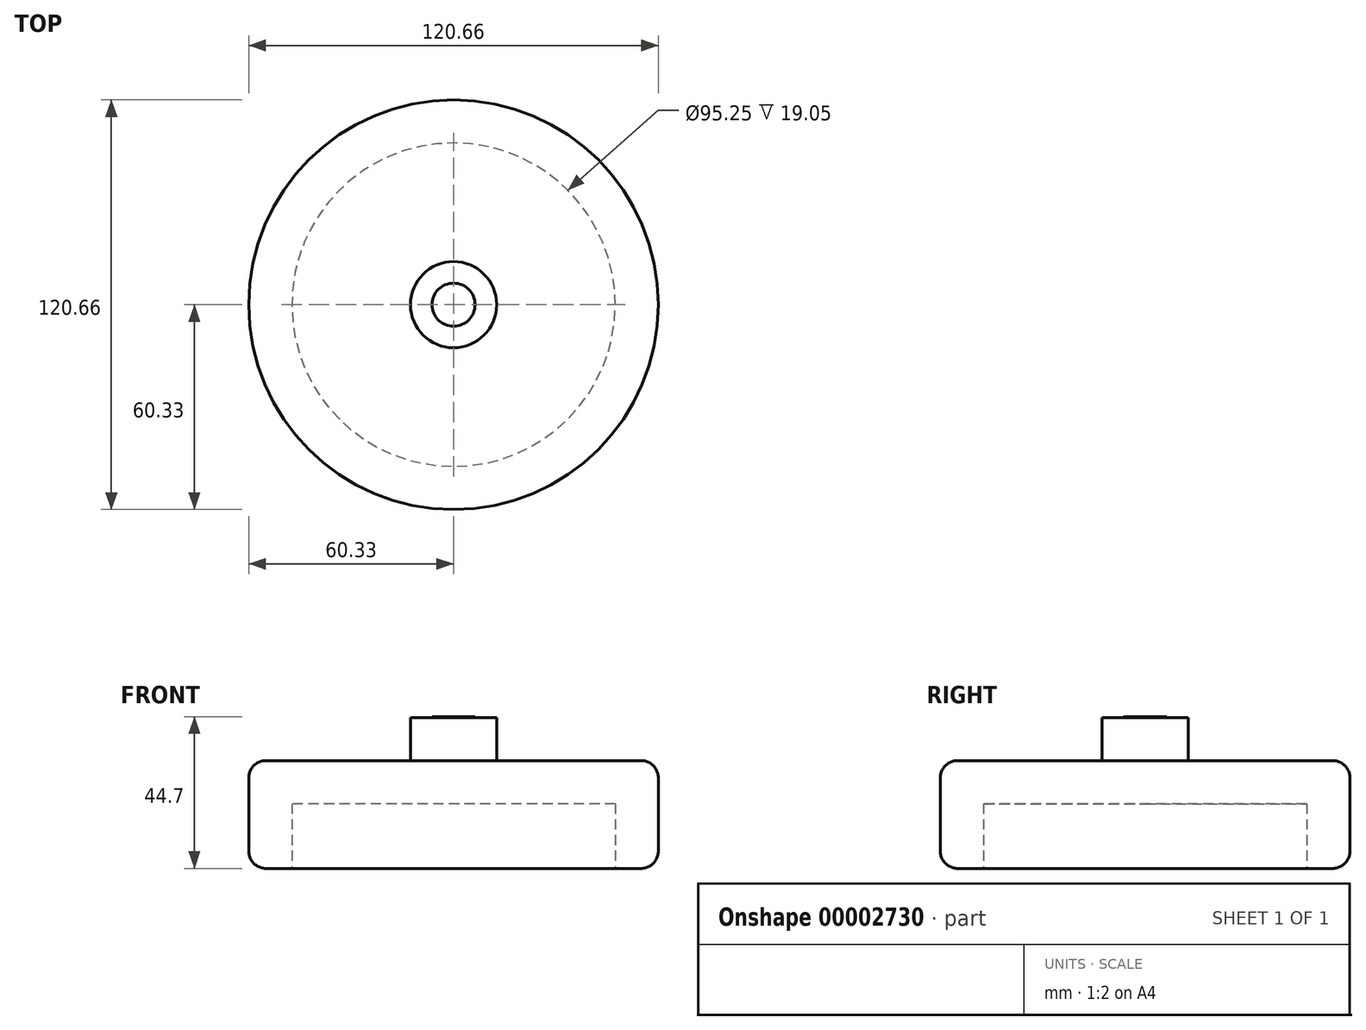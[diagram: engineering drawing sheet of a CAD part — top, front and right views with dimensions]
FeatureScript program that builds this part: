
annotation { "Feature Type Name" : "Feature", "Feature Type Description" : "" }
export const myFeature = defineFeature(function(context is Context, id is Id, definition is map)
    precondition{}
    {
        {
            var Q0;
            Q0=qCreatedBy(makeId("Top.planeOp"),FACE);
            var sketch = newSketch(context, id + "F0", { "sketchPlane" : qUnion([Q0])});
            skCircle(sketch, "E0", {"center": v(0, 0) * mm, "radius": 60.33 * mm});
            skSolve(sketch);
        }
        {
            var Q0;
            Q0=qCreatedBy(makeId("Top.planeOp"),FACE);
            var sketch = newSketch(context, id + "F1", { "sketchPlane" : qUnion([Q0])});
            skCircle(sketch, "E1", {"center": v(0, 0) * mm, "radius": 12.7 * mm});
            skSolve(sketch);
        }
        {
            var Q0;
            Q0=qCreatedBy(makeId("Top.planeOp"),FACE);
            var sketch = newSketch(context, id + "F2", { "sketchPlane" : qUnion([Q0])});
            skCircle(sketch, "E2", {"center": v(0, 0) * mm, "radius": 6.35 * mm});
            skSolve(sketch);
        }
        {
            var Q0;
            Q0=makeQuery(id+"F0.imprint","IMPRINT",FACE,{"disambiguationData":[TD([[makeQuery(id+"F0.imprint","IMPRINT",EDGE,{"derivedFrom":sQuery(id+"F0.wireOp",EDGE,"E0")}),1.0]])]});
            extrude(context, id + "F3", {"entities" : qUnion([Q0]), "depth" : 31.75 * mm});
        }
        {
            var Q0;
            Q0=makeQuery(id+"F1.imprint","IMPRINT",FACE,{"disambiguationData":[TD([[makeQuery(id+"F1.imprint","IMPRINT",EDGE,{"derivedFrom":sQuery(id+"F1.wireOp",EDGE,"E1")}),1.0]])]});
            extrude(context, id + "F4", {"entities" : qUnion([Q0]), "operationType" : NewBodyOperationType.ADD, "depth" : 44.45 * mm});
        }
        {
            var Q0;
            Q0=makeQuery(id+"F2.imprint","IMPRINT",FACE,{"disambiguationData":[TD([[makeQuery(id+"F2.imprint","IMPRINT",EDGE,{"derivedFrom":sQuery(id+"F2.wireOp",EDGE,"E2")}),1.0]])]});
            extrude(context, id + "F5", {"entities" : qUnion([Q0]), "operationType" : NewBodyOperationType.ADD, "depth" : 44.7 * mm});
        }
        {
            var Q0;
            Q0=makeQuery(id+"F3.opExtrude","CAP_FACE",FACE,{"disambiguationData":[OSD([sQuery(id+"F0.wireOp",EDGE,"E0")])],"isStart":true});
            shell(context, id + "F6", {"entities" : qUnion([Q0]), "thickness" : 12.7 * mm});
        }
        {
            var Q0;
            Q0=makeQuery(id+"F3.opExtrude","CAP_EDGE",EDGE,{"disambiguationData":[OSD([sQuery(id+"F0.wireOp",EDGE,"E0")])],"isStart":true});
            var Q1;
            Q1=makeQuery(id+"F3.opExtrude","CAP_EDGE",EDGE,{"disambiguationData":[OSD([sQuery(id+"F0.wireOp",EDGE,"E0")])],"isStart":false});
            fillet(context, id + "F7", {"entities" : qUnion([Q0, Q1]), "radius" : 5.08 * mm, "tangentPropagation" : true, "allowEdgeOverflow" : false});
        }
    });
